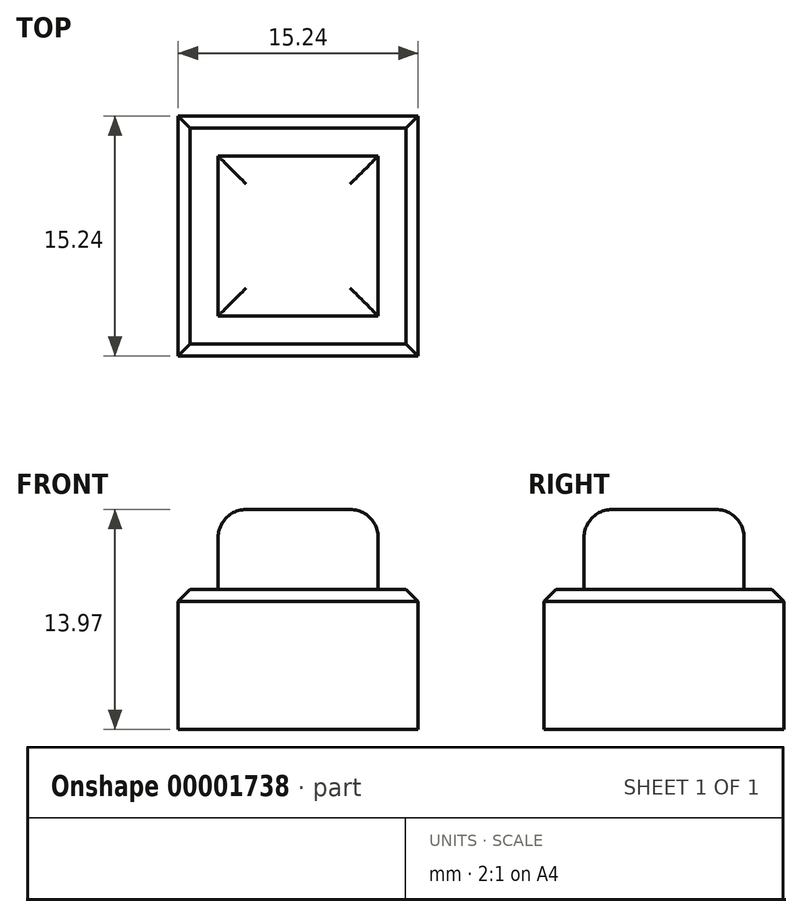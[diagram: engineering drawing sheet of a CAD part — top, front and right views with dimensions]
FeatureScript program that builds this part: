
annotation { "Feature Type Name" : "Feature", "Feature Type Description" : "" }
export const myFeature = defineFeature(function(context is Context, id is Id, definition is map)
    precondition{}
    {
        {
            var Q0;
            Q0=qCreatedBy(makeId("Top.planeOp"),FACE);
            var sketch = newSketch(context, id + "F0", { "sketchPlane" : qUnion([Q0])});
            skLineSegment(sketch, "E0.rect.bottom", {"start": v(7.62, -7.62) * mm, "end": v(-7.62, -7.62) * mm});
            skLineSegment(sketch, "E0.rect.top", {"start": v(7.62, 7.62) * mm, "end": v(-7.62, 7.62) * mm});
            skLineSegment(sketch, "E0.rect.left", {"start": v(7.62, -7.62) * mm, "end": v(7.62, 7.62) * mm});
            skLineSegment(sketch, "E0.rect.right", {"start": v(-7.62, -7.62) * mm, "end": v(-7.62, 7.62) * mm});
            skPoint(sketch, "E0.rect.middle", {"position": v(0, 0) * mm});
            skSolve(sketch);
        }
        {
            var Q0;
            Q0=makeQuery(id+"F0.imprint","IMPRINT",FACE,{"disambiguationData":[TD([[makeQuery(id+"F0.imprint","IMPRINT",EDGE,{"derivedFrom":sQuery(id+"F0.wireOp",EDGE,"E0.rect.bottom")}),-1.0]])]});
            extrude(context, id + "F1", {"entities" : qUnion([Q0]), "depth" : 8.9 * mm});
        }
        {
            var Q0;
            Q0=makeQuery(id+"F1.opExtrude","CAP_EDGE",EDGE,{"disambiguationData":[OSD([sQuery(id+"F0.wireOp",EDGE,"E0.rect.left")])],"isStart":false});
            var Q1;
            Q1=makeQuery(id+"F1.opExtrude","CAP_EDGE",EDGE,{"disambiguationData":[OSD([sQuery(id+"F0.wireOp",EDGE,"E0.rect.bottom")])],"isStart":false});
            var Q2;
            Q2=makeQuery(id+"F1.opExtrude","CAP_EDGE",EDGE,{"disambiguationData":[OSD([sQuery(id+"F0.wireOp",EDGE,"E0.rect.right")])],"isStart":false});
            var Q3;
            Q3=makeQuery(id+"F1.opExtrude","CAP_EDGE",EDGE,{"disambiguationData":[OSD([sQuery(id+"F0.wireOp",EDGE,"E0.rect.top")])],"isStart":false});
            chamfer(context, id + "F2", {"entities" : qUnion([Q0, Q1, Q2, Q3]), "width" : 0.76 * mm, "tangentPropagation" : true});
        }
        {
            var Q0;
            Q0=makeQuery(id+"F1.opExtrude","CAP_FACE",FACE,{"disambiguationData":[OSD([sQuery(id+"F0.wireOp",EDGE,"E0.rect.bottom"),sQuery(id+"F0.wireOp",EDGE,"E0.rect.top"),sQuery(id+"F0.wireOp",EDGE,"E0.rect.left"),sQuery(id+"F0.wireOp",EDGE,"E0.rect.right")])],"isStart":false});
            var sketch = newSketch(context, id + "F3", { "sketchPlane" : qUnion([Q0])});
            skLineSegment(sketch, "E1.rect.bottom", {"start": v(5.08, -5.08) * mm, "end": v(-5.08, -5.08) * mm});
            skLineSegment(sketch, "E1.rect.top", {"start": v(5.08, 5.08) * mm, "end": v(-5.08, 5.08) * mm});
            skLineSegment(sketch, "E1.rect.left", {"start": v(5.08, -5.08) * mm, "end": v(5.08, 5.08) * mm});
            skLineSegment(sketch, "E1.rect.right", {"start": v(-5.08, -5.08) * mm, "end": v(-5.08, 5.08) * mm});
            skPoint(sketch, "E1.rect.middle", {"position": v(0, 0) * mm});
            skSolve(sketch);
        }
        {
            var Q0;
            Q0 = qSketchRegion(id + "F3", true);
            extrude(context, id + "F4", {"entities" : qUnion([Q0]), "depth" : 5.08 * mm});
        }
        {
            var Q0;
            Q0=makeQuery(id+"F4.opExtrude","CAP_FACE",FACE,{"disambiguationData":[OSD([sQuery(id+"F3.wireOp",EDGE,"E1.rect.bottom"),sQuery(id+"F3.wireOp",EDGE,"E1.rect.top"),sQuery(id+"F3.wireOp",EDGE,"E1.rect.left"),sQuery(id+"F3.wireOp",EDGE,"E1.rect.right")])],"isStart":false});
            fillet(context, id + "F5", {"entities" : qUnion([Q0]), "radius" : 1.78 * mm, "tangentPropagation" : true, "allowEdgeOverflow" : false});
        }
    });
